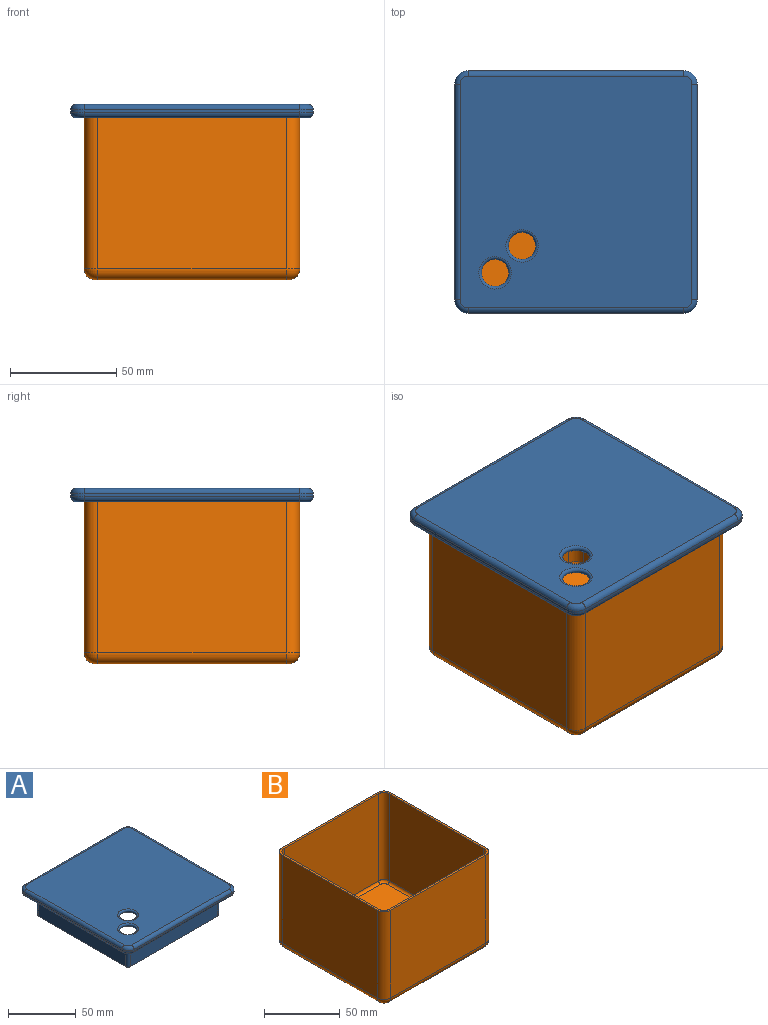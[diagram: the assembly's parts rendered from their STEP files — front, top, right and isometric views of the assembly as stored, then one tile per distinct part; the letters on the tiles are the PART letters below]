
ASSEMBLY  parts=2 mates=1
PART A: 55 faces, bbox 115.3x115.3x25.4 mm
  f0: plane 95.89x95.89mm, normal (0,0,-1), area 943mm2, adj f11,f12,f13,f14,f15,f16,f17,f18
  f1: plane 101.6x1.27mm, normal (1,0,0), area 129mm2, adj f7,f10,f40,f45
  f2: plane 101.6x1.27mm, normal (0,1,0), area 129mm2, adj f7,f8,f44,f48
  f3: plane 101.6x1.27mm, normal (-1,0,0), area 129mm2, adj f8,f9,f41,f52
  f4: plane 101.6x1.27mm, normal (0,-1,0), area 129mm2, adj f9,f10,f37,f49
  f5: plane 109.22x109.22mm, normal (0,0,-1), area 2601.7mm2, adj f11,f12,f13,f14,f15,f16,f17,f18
  f6: plane 109.22x109.22mm, normal (0,0,1), area 11551.7mm2, adj f45,f46,f47,f48,f49,f50,f51,f52
  f7: cylinder r=6.35mm len=6.35mm, axis (0,0,-1), area 12.7mm2, adj f1,f2,f42,f46
  f8: cylinder r=6.35mm len=6.35mm, axis (0,0,1), area 12.7mm2, adj f2,f3,f43,f50
  f9: cylinder r=6.35mm len=6.35mm, axis (0,0,-1), area 12.7mm2, adj f3,f4,f39,f51
  f10: cylinder r=6.35mm len=6.35mm, axis (0,0,1), area 12.7mm2, adj f1,f4,f38,f47
  f11: cone r=2.54mm half-angle=1deg, axis (0,0,1), area 81mm2, adj f0,f5,f12,f18
  f12: plane 90.81x19.05mm, normal (1,0,-0.02), area 1730.1mm2, adj f0,f5,f11,f13
  f13: cone r=2.54mm half-angle=1deg, axis (0,0,1), area 81mm2, adj f0,f5,f12,f14
  f14: plane 90.81x19.05mm, normal (0,1,-0.02), area 1730.1mm2, adj f0,f5,f13,f15
  f15: cone r=2.54mm half-angle=1deg, axis (0,0,1), area 81mm2, adj f0,f5,f14,f16
  f16: plane 90.81x19.05mm, normal (-1,0,-0.02), area 1730.1mm2, adj f0,f5,f15,f17
  f17: cone r=2.54mm half-angle=1deg, axis (0,0,1), area 81mm2, adj f0,f5,f16,f18
  f18: plane 90.81x19.05mm, normal (0,-1,-0.02), area 1730.1mm2, adj f0,f5,f11,f17
  f19: plane 101.6x1.27mm, normal (-1,0,0), area 129mm2, adj f23,f24,f25,f28
  f20: plane 101.6x1.27mm, normal (0,-1,0), area 129mm2, adj f23,f24,f25,f26
  f21: plane 101.6x1.27mm, normal (1,0,0), area 129mm2, adj f23,f24,f26,f27
  f22: plane 101.6x1.27mm, normal (0,1,0), area 129mm2, adj f23,f24,f27,f28
  f23: plane 109.22x109.22mm, normal (0,0,1), area 3533.8mm2, adj f19,f20,f21,f22,f25,f26,f27,f28
  f24: plane 109.22x109.22mm, normal (0,0,-1), area 11551.7mm2, adj f19,f20,f21,f22,f25,f26,f27,f28
  f25: cylinder r=3.81mm len=3.81mm, axis (0,0,-1), area 7.6mm2, adj f19,f20,f23,f24
  f26: cylinder r=3.81mm len=3.81mm, axis (0,0,1), area 7.6mm2, adj f20,f21,f23,f24
  f27: cylinder r=3.81mm len=3.81mm, axis (0,0,-1), area 7.6mm2, adj f21,f22,f23,f24
  f28: cylinder r=3.81mm len=3.81mm, axis (0,0,1), area 7.6mm2, adj f19,f22,f23,f24
  f29: cone r=0mm half-angle=1deg, axis (0,0,1), area 6.4mm2, adj f23,f30,f36
  f30: plane 90.81x21.59mm, normal (-1,0,0.02), area 1960.8mm2, adj f0,f23,f29,f31,f32,f36
  f31: cone r=0mm half-angle=1deg, axis (0,0,1), area 6.4mm2, adj f23,f30,f32
  f32: plane 90.81x21.59mm, normal (0,-1,0.02), area 1960.8mm2, adj f0,f23,f30,f31,f33,f34
  f33: cone r=0mm half-angle=1deg, axis (0,0,1), area 6.4mm2, adj f23,f32,f34
  f34: plane 90.81x21.59mm, normal (1,0,0.02), area 1960.8mm2, adj f0,f23,f32,f33,f35,f36
  f35: cone r=0mm half-angle=1deg, axis (0,0,1), area 6.4mm2, adj f23,f34,f36
  f36: plane 90.81x21.59mm, normal (0,1,0.02), area 1960.8mm2, adj f0,f23,f29,f30,f34,f35
  f37: cylinder r=2.54mm len=101.6mm, axis (-1,0,0), area 405.4mm2, adj f4,f5,f38,f39
  f38: torus R=3.81mm, axis (0,0,1), area 34mm2, adj f5,f10,f37,f40
  f39: torus R=3.81mm, axis (0,0,1), area 34mm2, adj f5,f9,f37,f41
  f40: cylinder r=2.54mm len=101.6mm, axis (0,-1,0), area 405.4mm2, adj f1,f5,f38,f42
  f41: cylinder r=2.54mm len=101.6mm, axis (0,1,0), area 405.4mm2, adj f3,f5,f39,f43
  f42: torus R=3.81mm, axis (0,0,1), area 34mm2, adj f5,f7,f40,f44
  f43: torus R=3.81mm, axis (0,0,1), area 34mm2, adj f5,f8,f41,f44
  f44: cylinder r=2.54mm len=101.6mm, axis (1,0,0), area 405.4mm2, adj f2,f5,f42,f43
  f45: cylinder r=2.54mm len=101.6mm, axis (0,1,0), area 405.4mm2, adj f1,f6,f46,f47
  f46: torus R=3.81mm, axis (0,0,1), area 34mm2, adj f6,f7,f45,f48
  f47: torus R=3.81mm, axis (0,0,1), area 34mm2, adj f6,f10,f45,f49
  f48: cylinder r=2.54mm len=101.6mm, axis (-1,0,0), area 405.4mm2, adj f2,f6,f46,f50
  f49: cylinder r=2.54mm len=101.6mm, axis (1,0,0), area 405.4mm2, adj f4,f6,f47,f51
  f50: torus R=3.81mm, axis (0,0,1), area 34mm2, adj f6,f8,f48,f52
  f51: torus R=3.81mm, axis (0,0,1), area 34mm2, adj f6,f9,f49,f52
  f52: cylinder r=2.54mm len=101.6mm, axis (0,-1,0), area 405.4mm2, adj f3,f6,f50,f51
  f53: torus R=7.62mm, axis (0,0,1), area 170.8mm2, adj f6,f24
  f54: torus R=7.62mm, axis (0,0,1), area 170.8mm2, adj f6,f24
PART B: 35 faces, bbox 101.6x101.6x76.2 mm
  f0: plane 88.9x71.12mm, normal (1,0,0), area 6322.6mm2, adj f1,f7,f8,f34
  f1: cylinder r=6.35mm len=71.12mm, axis (0,0,-1), area 709.4mm2, adj f0,f2,f8,f32
  f2: plane 88.9x71.12mm, normal (0,1,0), area 6322.6mm2, adj f1,f3,f8,f30
  f3: cylinder r=6.35mm len=71.12mm, axis (0,0,-1), area 709.4mm2, adj f2,f4,f8,f28
  f4: plane 88.9x71.12mm, normal (-1,0,0), area 6322.6mm2, adj f3,f5,f8,f27
  f5: cylinder r=6.35mm len=71.12mm, axis (0,0,-1), area 709.4mm2, adj f4,f6,f8,f29
  f6: plane 88.9x71.12mm, normal (0,-1,0), area 6322.6mm2, adj f5,f7,f8,f31
  f7: cylinder r=6.35mm len=71.12mm, axis (0,0,-1), area 709.4mm2, adj f0,f6,f8,f33
  f8: plane 101.6x101.6mm, normal (0,0,1), area 622.6mm2, adj f0,f1,f2,f3,f4,f5,f6,f7
  f9: plane 91.44x91.44mm, normal (0,0,-1), area 8359.9mm2, adj f27,f28,f29,f30,f31,f32,f33,f34
  f10: plane 88.27x70.49mm, normal (1,0,0), area 6221.4mm2, adj f8,f11,f17,f26
  f11: cylinder r=5.08mm len=70.49mm, axis (0,0,1), area 562.4mm2, adj f8,f10,f12,f25
  f12: plane 88.27x70.49mm, normal (0,1,0), area 6221.4mm2, adj f8,f11,f13,f23
  f13: cylinder r=5.08mm len=70.49mm, axis (0,0,1), area 562.4mm2, adj f8,f12,f14,f21
  f14: plane 88.27x70.49mm, normal (-1,0,0), area 6221.4mm2, adj f8,f13,f15,f19
  f15: cylinder r=5.08mm len=70.49mm, axis (0,0,1), area 562.4mm2, adj f8,f14,f16,f20
  f16: plane 88.27x70.49mm, normal (0,-1,0), area 6221.4mm2, adj f8,f15,f17,f22
  f17: cylinder r=5.08mm len=70.49mm, axis (0,0,1), area 562.4mm2, adj f8,f10,f16,f24
  f18: plane 94.62x94.62mm, normal (0,0,1), area 8943.3mm2, adj f19,f20,f21,f22,f23,f24,f25,f26
  f19: cylinder r=1.91mm len=88.27mm, axis (0,1,0), area 264.1mm2, adj f14,f18,f20,f21
  f20: torus R=3.17mm, axis (0,0,1), area 20.6mm2, adj f15,f18,f19,f22
  f21: torus R=3.17mm, axis (0,0,1), area 20.6mm2, adj f13,f18,f19,f23
  f22: cylinder r=1.91mm len=88.27mm, axis (-1,0,0), area 264.1mm2, adj f16,f18,f20,f24
  f23: cylinder r=1.91mm len=88.27mm, axis (1,0,0), area 264.1mm2, adj f12,f18,f21,f25
  f24: torus R=3.17mm, axis (0,0,1), area 20.6mm2, adj f17,f18,f22,f26
  f25: torus R=3.17mm, axis (0,0,1), area 20.6mm2, adj f11,f18,f23,f26
  f26: cylinder r=1.91mm len=88.27mm, axis (0,-1,0), area 264.1mm2, adj f10,f18,f24,f25
  f27: cylinder r=5.08mm len=88.9mm, axis (0,-1,0), area 709.4mm2, adj f4,f9,f28,f29
  f28: torus R=1.27mm, axis (0,0,1), area 56.5mm2, adj f3,f9,f27,f30
  f29: torus R=1.27mm, axis (0,0,1), area 56.5mm2, adj f5,f9,f27,f31
  f30: cylinder r=5.08mm len=88.9mm, axis (-1,0,0), area 709.4mm2, adj f2,f9,f28,f32
  f31: cylinder r=5.08mm len=88.9mm, axis (1,0,0), area 709.4mm2, adj f6,f9,f29,f33
  f32: torus R=1.27mm, axis (0,0,1), area 56.5mm2, adj f1,f9,f30,f34
  f33: torus R=1.27mm, axis (0,0,1), area 56.5mm2, adj f7,f9,f31,f34
  f34: cylinder r=5.08mm len=88.9mm, axis (0,1,0), area 709.4mm2, adj f0,f9,f32,f33
PLACE A t=(-38.52,-3.3,47.47)mm
PLACE B t=(-38.52,-3.3,-9.68)mm
MATE planar A.f5 <-> B.f8  axis (0,0,-1) through (-38.52,-3.3,66.52)mm
